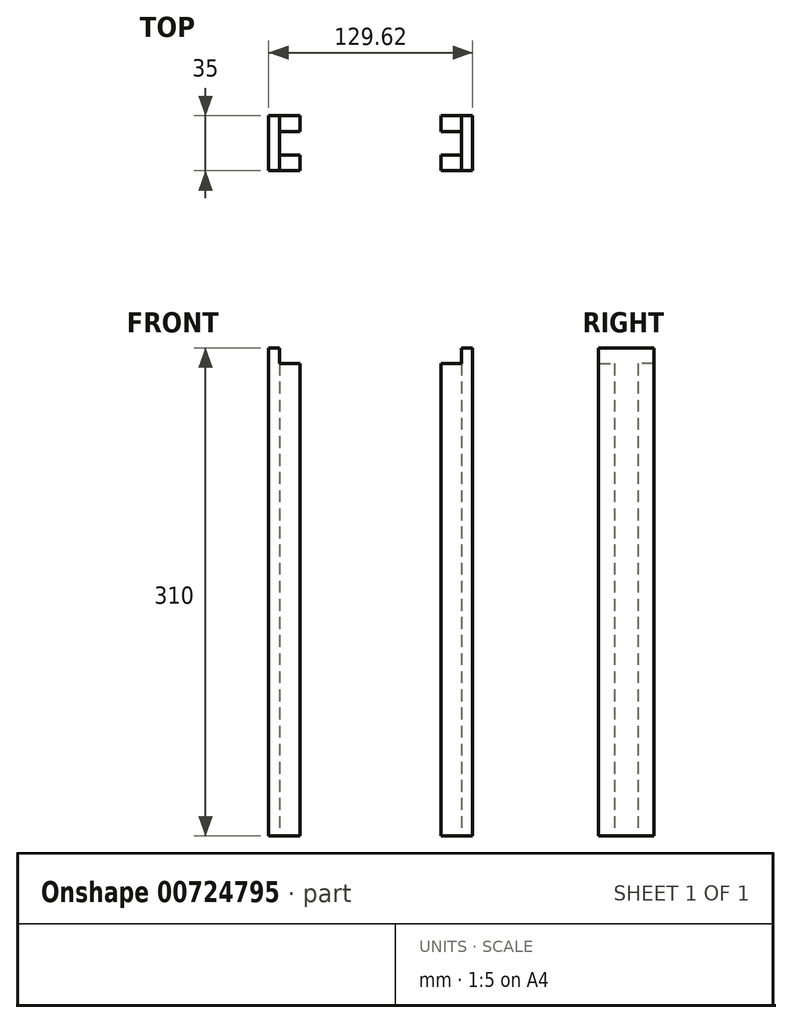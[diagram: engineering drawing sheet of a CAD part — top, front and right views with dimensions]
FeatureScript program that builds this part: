
annotation { "Feature Type Name" : "Feature", "Feature Type Description" : "" }
export const myFeature = defineFeature(function(context is Context, id is Id, definition is map)
    precondition{}
    {
        {
            var Q0;
            Q0=qCreatedBy(makeId("Top.planeOp"),FACE);
            var sketch = newSketch(context, id + "F0", { "sketchPlane" : qUnion([Q0])});
            skLineSegment(sketch, "E0", {"start": v(-44.81, 0) * mm, "end": v(-44.81, 10) * mm});
            skLineSegment(sketch, "E1", {"start": v(-44.81, 10) * mm, "end": v(-44.81, 0) * mm});
            skLineSegment(sketch, "E2", {"start": v(-64.81, 0) * mm, "end": v(-64.81, 35) * mm});
            skLineSegment(sketch, "E3", {"start": v(-64.81, 35) * mm, "end": v(-44.81, 35) * mm});
            skLineSegment(sketch, "E4", {"start": v(-44.81, 35) * mm, "end": v(-44.81, 25) * mm});
            skLineSegment(sketch, "E5", {"start": v(-44.81, 25) * mm, "end": v(-57.81, 25) * mm});
            skLineSegment(sketch, "E6", {"start": v(-57.81, 25) * mm, "end": v(-57.81, 10) * mm});
            skLineSegment(sketch, "E7", {"start": v(-57.81, 10) * mm, "end": v(-44.81, 10) * mm});
            skLineSegment(sketch, "E8", {"start": v(-64.81, 0) * mm, "end": v(-44.81, 0) * mm});
            skSolve(sketch);
        }
        {
            var Q0;
            Q0 = qSketchRegion(id + "F0", true);
            extrude(context, id + "F1", {"entities" : qUnion([Q0]), "depth" : 300 * mm, "offsetDistance" : 25 * mm});
        }
        {
            var Q0;
            Q0=makeQuery(id+"F1.opExtrude","CAP_FACE",FACE,{"disambiguationData":[OSD([sQuery(id+"F0.wireOp",EDGE,"E1"),sQuery(id+"F0.wireOp",EDGE,"E2"),sQuery(id+"F0.wireOp",EDGE,"E3"),sQuery(id+"F0.wireOp",EDGE,"E4"),sQuery(id+"F0.wireOp",EDGE,"E5"),sQuery(id+"F0.wireOp",EDGE,"E6"),sQuery(id+"F0.wireOp",EDGE,"E7"),sQuery(id+"F0.wireOp",EDGE,"E8")])],"isStart":false});
            var sketch = newSketch(context, id + "F2", { "sketchPlane" : qUnion([Q0])});
            skLineSegment(sketch, "E9", {"start": v(-57.81, 25) * mm, "end": v(-57.81, 35) * mm});
            skLineSegment(sketch, "E10", {"start": v(-57.81, 35) * mm, "end": v(-57.81, 10) * mm});
            skLineSegment(sketch, "E11", {"start": v(-57.81, 10) * mm, "end": v(-57.81, 0) * mm});
            skLineSegment(sketch, "E12", {"start": v(-57.81, 0) * mm, "end": v(-64.81, 0) * mm});
            skLineSegment(sketch, "E13", {"start": v(-64.81, 0) * mm, "end": v(-64.81, 35) * mm});
            skLineSegment(sketch, "E14", {"start": v(-64.81, 35) * mm, "end": v(-57.81, 35) * mm});
            skSolve(sketch);
        }
        {
            var Q0;
            Q0 = qSketchRegion(id + "F2", true);
            var Q1;
            {var subQ0=sQuery(id+"F2.wireOp",EDGE,"E11");Q1=makeQuery(id+"F2.imprint","IMPRINT",FACE,{"disambiguationData":[TD([[makeQuery(id+"F2.imprint","IMPRINT",EDGE,{"derivedFrom":subQ0}),-1.0]])]});}
            extrude(context, id + "F3", {"entities" : qUnion([Q0, Q1]), "operationType" : NewBodyOperationType.ADD, "depth" : 10 * mm, "offsetDistance" : 25 * mm});
        }
        {
            var Q0;
            Q0=makeQuery(id+"F1.opExtrude","SWEPT_BODY",BODY,{"disambiguationData":[OSD([sQuery(id+"F0.wireOp",EDGE,"E1"),sQuery(id+"F0.wireOp",EDGE,"E2"),sQuery(id+"F0.wireOp",EDGE,"E3"),sQuery(id+"F0.wireOp",EDGE,"E4"),sQuery(id+"F0.wireOp",EDGE,"E5"),sQuery(id+"F0.wireOp",EDGE,"E6"),sQuery(id+"F0.wireOp",EDGE,"E7"),sQuery(id+"F0.wireOp",EDGE,"E8")])]});
            var Q1;
            Q1=qCreatedBy(makeId("Right.planeOp"),FACE);
            mirror(context, id + "F4", {"entities" : qUnion([Q0]), "mirrorPlane" : qUnion([Q1])});
        }
    });
